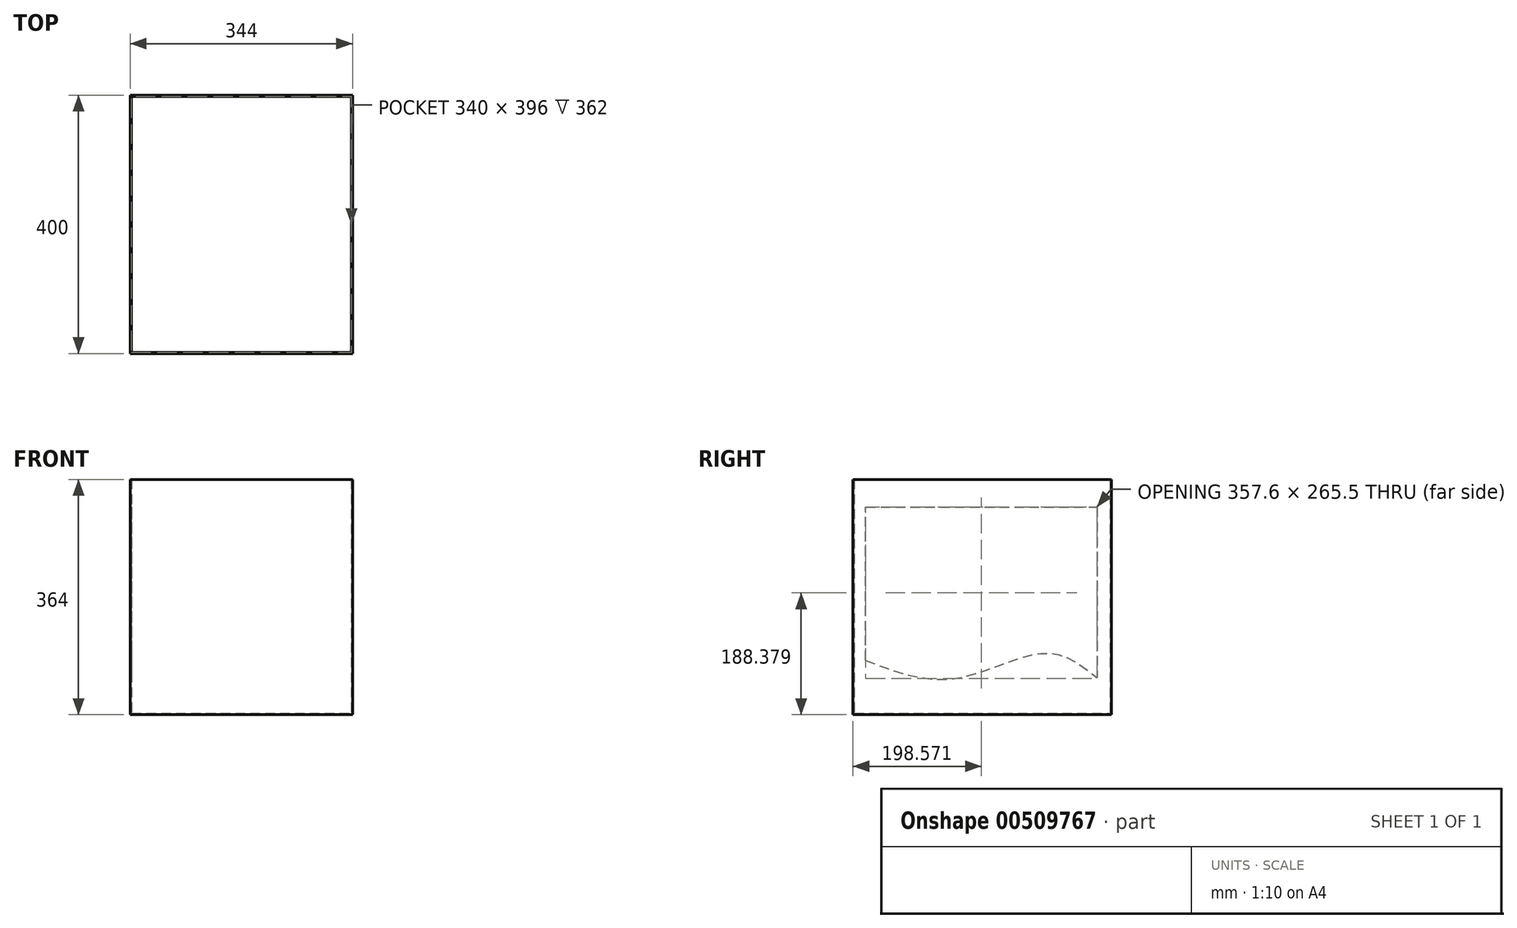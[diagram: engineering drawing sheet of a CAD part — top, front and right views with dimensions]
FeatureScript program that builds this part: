
annotation { "Feature Type Name" : "Feature", "Feature Type Description" : "" }
export const myFeature = defineFeature(function(context is Context, id is Id, definition is map)
    precondition{}
    {
        {
            var Q0;
            Q0=qCreatedBy(makeId("Front.planeOp"),FACE);
            var sketch = newSketch(context, id + "F0", { "sketchPlane" : qUnion([Q0])});
            skLineSegment(sketch, "E0.bottom", {"start": v(0, 0) * mm, "end": v(344, 0) * mm});
            skLineSegment(sketch, "E0.top", {"start": v(0, -364) * mm, "end": v(344, -364) * mm});
            skLineSegment(sketch, "E0.left", {"start": v(0, 0) * mm, "end": v(0, -364) * mm});
            skLineSegment(sketch, "E0.right", {"start": v(344, 0) * mm, "end": v(344, -364) * mm});
            skSolve(sketch);
        }
        {
            var Q0;
            Q0 = qSketchRegion(id + "F0", true);
            extrude(context, id + "F1", {"entities" : qUnion([Q0]), "depth" : 400 * mm});
        }
        {
            var Q0;
            Q0=makeQuery(id+"F1.opExtrude","SWEPT_FACE",FACE,{"disambiguationData":[OSD([sQuery(id+"F0.wireOp",EDGE,"E0.bottom")])]});
            shell(context, id + "F2", {"entities" : qUnion([Q0]), "thickness" : 2 * mm});
        }
        {
            var Q0;
            Q0=makeQuery(id+"F1.opExtrude","SWEPT_FACE",FACE,{"disambiguationData":[OSD([sQuery(id+"F0.wireOp",EDGE,"E0.right")])]});
            var sketch = newSketch(context, id + "F3", { "sketchPlane" : qUnion([Q0])});
            skFitSpline(sketch, "E1", {"points": [v(-380.23, -279.9) * mm, v(-242.43, -308.14) * mm, v(-101.18, -268.87) * mm, v(-22.63, -306.76) * mm], "startDerivative": vector(378.42, -147.54) * mm, "endDerivative": vector(254.64, -203.27) * mm});
            skLineSegment(sketch, "E2", {"start": v(-380.23, -279.9) * mm, "end": v(-380.23, -42.87) * mm});
            skLineSegment(sketch, "E3", {"start": v(-380.23, -42.87) * mm, "end": v(-22.63, -42.87) * mm});
            skLineSegment(sketch, "E4", {"start": v(-22.63, -42.87) * mm, "end": v(-22.63, -306.76) * mm});
            skSolve(sketch);
        }
        {
            var Q0;
            Q0 = qSketchRegion(id + "F3", true);
            extrude(context, id + "F4", {"entities" : qUnion([Q0]), "operationType" : NewBodyOperationType.REMOVE, "endBound" : BoundingType.THROUGH_ALL, "oppositeDirection" : true, "depth" : 400 * mm, "hasSecondDirection" : true, "secondDirectionOppositeDirection" : true, "secondDirectionDepth" : 25 * mm});
        }
    });
